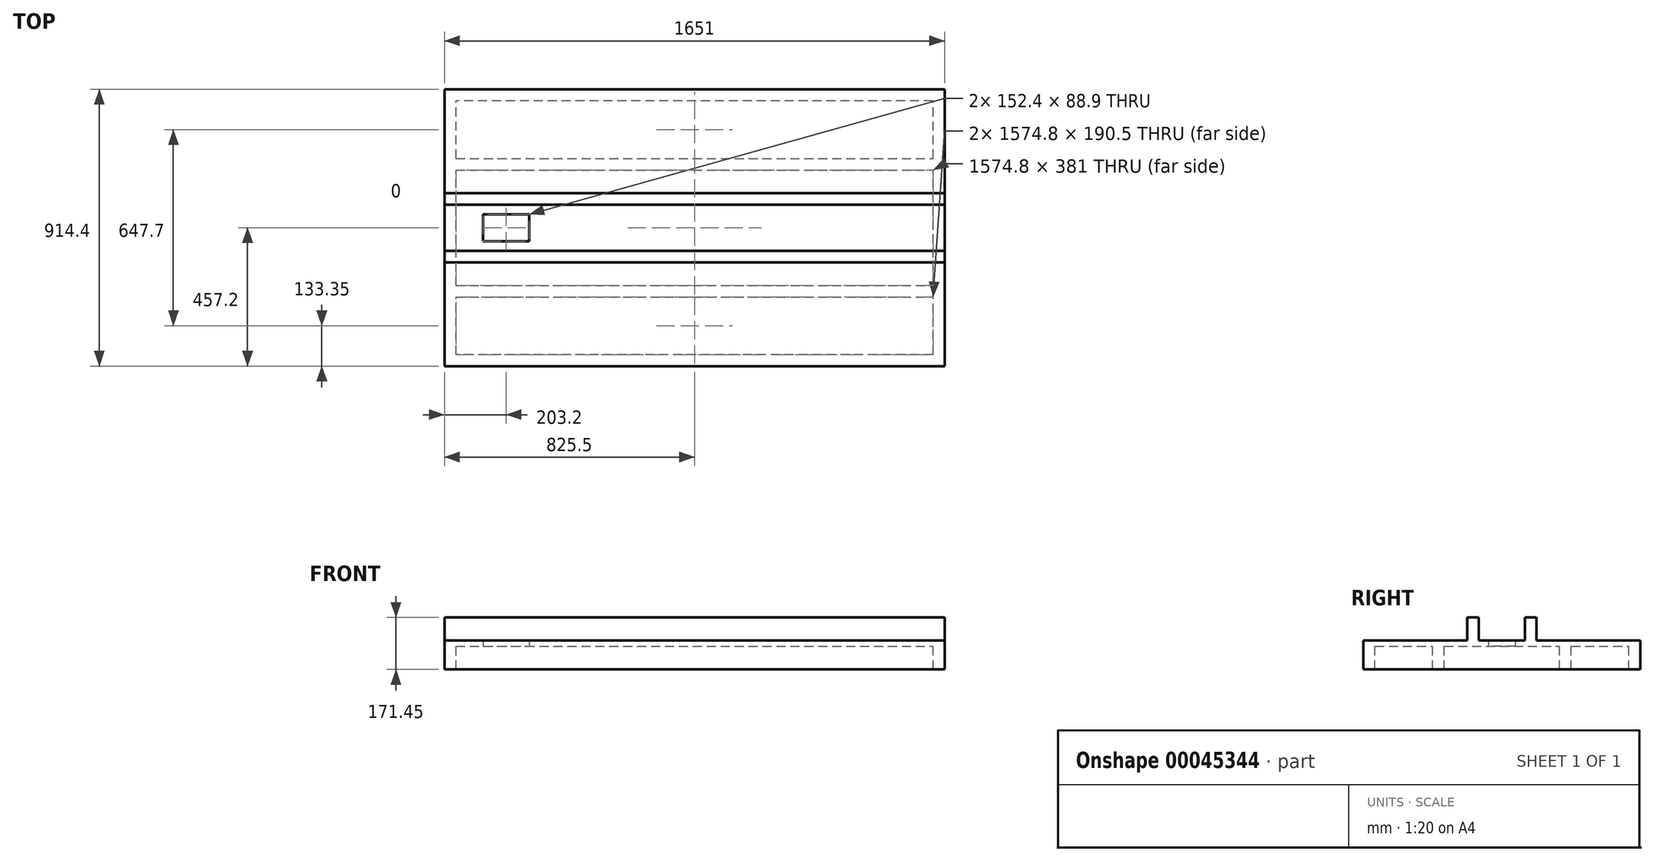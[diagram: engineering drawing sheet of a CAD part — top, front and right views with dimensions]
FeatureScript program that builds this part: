
annotation { "Feature Type Name" : "Feature", "Feature Type Description" : "" }
export const myFeature = defineFeature(function(context is Context, id is Id, definition is map)
    precondition{}
    {
        {
            var Q0;
            Q0=qCreatedBy(makeId("Top.planeOp"),FACE);
            var sketch = newSketch(context, id + "F0", { "sketchPlane" : qUnion([Q0])});
            skLineSegment(sketch, "E0.rect.bottom", {"start": v(825.5, 457.2) * mm, "end": v(-825.5, 457.2) * mm});
            skLineSegment(sketch, "E0.rect.top", {"start": v(825.5, -457.2) * mm, "end": v(-825.5, -457.2) * mm});
            skLineSegment(sketch, "E0.rect.left", {"start": v(825.5, 457.2) * mm, "end": v(825.5, -457.2) * mm});
            skLineSegment(sketch, "E0.rect.right", {"start": v(-825.5, 457.2) * mm, "end": v(-825.5, -457.2) * mm});
            skPoint(sketch, "E0.rect.middle", {"position": v(0, 0) * mm});
            skLineSegment(sketch, "E1", {"start": v(-825.5, 0) * mm, "end": v(-698.5, 0) * mm, "construction": true});
            skPoint(sketch, "E1.endSnap0", {"position": v(-825.5, 0) * mm});
            skLineSegment(sketch, "E2.rect.bottom", {"start": v(-698.5, 44.45) * mm, "end": v(-546.1, 44.45) * mm});
            skLineSegment(sketch, "E2.rect.top", {"start": v(-698.5, -44.45) * mm, "end": v(-546.1, -44.45) * mm});
            skLineSegment(sketch, "E2.rect.left", {"start": v(-698.5, 44.45) * mm, "end": v(-698.5, -44.45) * mm});
            skLineSegment(sketch, "E2.rect.right", {"start": v(-546.1, 44.45) * mm, "end": v(-546.1, -44.45) * mm});
            skPoint(sketch, "E2.rect.middle", {"position": v(-622.3, 0) * mm});
            skSolve(sketch);
        }
        {
            var Q0;
            Q0 = qSketchRegion(id + "F0", true);
            var Q1;
            Q1=makeQuery(id+"F0.imprint","IMPRINT",FACE,{"disambiguationData":[TD([[makeQuery(id+"F0.imprint","IMPRINT",EDGE,{"derivedFrom":sQuery(id+"F0.wireOp",EDGE,"E0.rect.bottom")}),1.0]])]});
            extrude(context, id + "F1", {"entities" : qUnion([Q0, Q1]), "depth" : 19.05 * mm});
        }
        {
            var Q0;
            Q0=makeQuery(id+"F1.opExtrude","CAP_FACE",FACE,{"disambiguationData":[OSD([sQuery(id+"F0.wireOp",EDGE,"E0.rect.bottom"),sQuery(id+"F0.wireOp",EDGE,"E0.rect.top"),sQuery(id+"F0.wireOp",EDGE,"E0.rect.left"),sQuery(id+"F0.wireOp",EDGE,"E0.rect.right"),sQuery(id+"F0.wireOp",EDGE,"E2.rect.bottom"),sQuery(id+"F0.wireOp",EDGE,"E2.rect.top"),sQuery(id+"F0.wireOp",EDGE,"E2.rect.left"),sQuery(id+"F0.wireOp",EDGE,"E2.rect.right")])],"isStart":false});
            var sketch = newSketch(context, id + "F2", { "sketchPlane" : qUnion([Q0])});
            skLineSegment(sketch, "E3.bottom", {"start": v(825.5, 76.2) * mm, "end": v(-825.5, 76.2) * mm});
            skLineSegment(sketch, "E3.top", {"start": v(825.5, 114.3) * mm, "end": v(-825.5, 114.3) * mm});
            skLineSegment(sketch, "E3.left", {"start": v(825.5, 76.2) * mm, "end": v(825.5, 114.3) * mm});
            skLineSegment(sketch, "E3.right", {"start": v(-825.5, 76.2) * mm, "end": v(-825.5, 114.3) * mm});
            skLineSegment(sketch, "E4", {"start": v(-825.5, 0) * mm, "end": v(825.5, 0) * mm, "construction": true});
            skLineSegment(sketch, "E5.bottom", {"start": v(-825.5, -76.2) * mm, "end": v(825.5, -76.2) * mm});
            skLineSegment(sketch, "E5.top", {"start": v(-825.5, -114.3) * mm, "end": v(825.5, -114.3) * mm});
            skLineSegment(sketch, "E5.left", {"start": v(-825.5, -76.2) * mm, "end": v(-825.5, -114.3) * mm});
            skLineSegment(sketch, "E5.right", {"start": v(825.5, -76.2) * mm, "end": v(825.5, -114.3) * mm});
            skSolve(sketch);
        }
        {
            var Q0;
            Q0 = qSketchRegion(id + "F2", true);
            extrude(context, id + "F3", {"entities" : qUnion([Q0]), "operationType" : NewBodyOperationType.ADD, "depth" : 76.2 * mm});
        }
        {
            var Q0;
            Q0=makeQuery(id+"F1.opExtrude","CAP_FACE",FACE,{"disambiguationData":[OSD([sQuery(id+"F0.wireOp",EDGE,"E0.rect.bottom"),sQuery(id+"F0.wireOp",EDGE,"E0.rect.top"),sQuery(id+"F0.wireOp",EDGE,"E0.rect.left"),sQuery(id+"F0.wireOp",EDGE,"E0.rect.right"),sQuery(id+"F0.wireOp",EDGE,"E2.rect.bottom"),sQuery(id+"F0.wireOp",EDGE,"E2.rect.top"),sQuery(id+"F0.wireOp",EDGE,"E2.rect.left"),sQuery(id+"F0.wireOp",EDGE,"E2.rect.right")])],"isStart":true});
            var sketch = newSketch(context, id + "F4", { "sketchPlane" : qUnion([Q0])});
            skLineSegment(sketch, "E6.rect.bottom", {"start": v(787.4, 419.1) * mm, "end": v(-787.4, 419.1) * mm});
            skLineSegment(sketch, "E6.rect.top", {"start": v(787.4, -419.1) * mm, "end": v(-787.4, -419.1) * mm});
            skLineSegment(sketch, "E6.rect.left", {"start": v(787.4, 419.1) * mm, "end": v(787.4, 228.6) * mm});
            skLineSegment(sketch, "E6.rect.right", {"start": v(-787.4, 419.1) * mm, "end": v(-787.4, 228.6) * mm});
            skPoint(sketch, "E6.rect.middle", {"position": v(0, 0) * mm});
            skLineSegment(sketch, "E7.rect.bottom", {"start": v(-825.5, -457.2) * mm, "end": v(825.5, -457.2) * mm});
            skLineSegment(sketch, "E7.rect.top", {"start": v(-825.5, 457.2) * mm, "end": v(825.5, 457.2) * mm});
            skLineSegment(sketch, "E7.rect.left", {"start": v(-825.5, -457.2) * mm, "end": v(-825.5, 457.2) * mm});
            skLineSegment(sketch, "E7.rect.right", {"start": v(825.5, -457.2) * mm, "end": v(825.5, 457.2) * mm});
            skLineSegment(sketch, "E8.bottom", {"start": v(-787.4, -190.5) * mm, "end": v(787.4, -190.5) * mm});
            skLineSegment(sketch, "E8.top", {"start": v(-787.4, -228.6) * mm, "end": v(787.4, -228.6) * mm});
            skLineSegment(sketch, "E9.bottom", {"start": v(-787.4, 190.5) * mm, "end": v(787.4, 190.5) * mm});
            skLineSegment(sketch, "E9.top", {"start": v(-787.4, 228.6) * mm, "end": v(787.4, 228.6) * mm});
            skLineSegment(sketch, "E9.right", {"start": v(787.4, 190.5) * mm, "end": v(787.4, 228.6) * mm});
            skLineSegment(sketch, "E10", {"start": v(-787.4, 0) * mm, "end": v(787.4, 0) * mm, "construction": true});
            skLineSegment(sketch, "E11.trimOffspring", {"start": v(-787.4, 190.5) * mm, "end": v(-787.4, -419.1) * mm});
            skLineSegment(sketch, "E12.trimOffspring", {"start": v(787.4, 190.5) * mm, "end": v(787.4, -419.1) * mm});
            skSolve(sketch);
        }
        {
            var Q0;
            Q0 = qSketchRegion(id + "F4", true);
            var Q1;
            {var subQ2=sQuery(id+"F4.wireOp",EDGE,"E8.bottom");Q1=makeQuery(id+"F4.imprint","IMPRINT",FACE,{"disambiguationData":[TD([[makeQuery(id+"F4.imprint","IMPRINT",EDGE,{"derivedFrom":subQ2}),-1.0]])]});}
            extrude(context, id + "F5", {"entities" : qUnion([Q0, Q1]), "operationType" : NewBodyOperationType.ADD, "depth" : 76.2 * mm});
        }
        {
            var Q0;
            Q0=makeQuery(id+"F1.opExtrude","SWEPT_BODY",BODY,{"disambiguationData":[OSD([sQuery(id+"F0.wireOp",EDGE,"E0.rect.bottom"),sQuery(id+"F0.wireOp",EDGE,"E0.rect.top"),sQuery(id+"F0.wireOp",EDGE,"E0.rect.left"),sQuery(id+"F0.wireOp",EDGE,"E0.rect.right"),sQuery(id+"F0.wireOp",EDGE,"E2.rect.bottom"),sQuery(id+"F0.wireOp",EDGE,"E2.rect.top"),sQuery(id+"F0.wireOp",EDGE,"E2.rect.left"),sQuery(id+"F0.wireOp",EDGE,"E2.rect.right")])]});
            transform(context, id + "F6", {"entities" : qUnion([Q0]), "transformType" : TransformType.TRANSLATION_3D, "dx" : 0 * mm, "dy" : 0 * mm, "dz" : 0 * mm, "makeCopy" : true});
        }
    });
